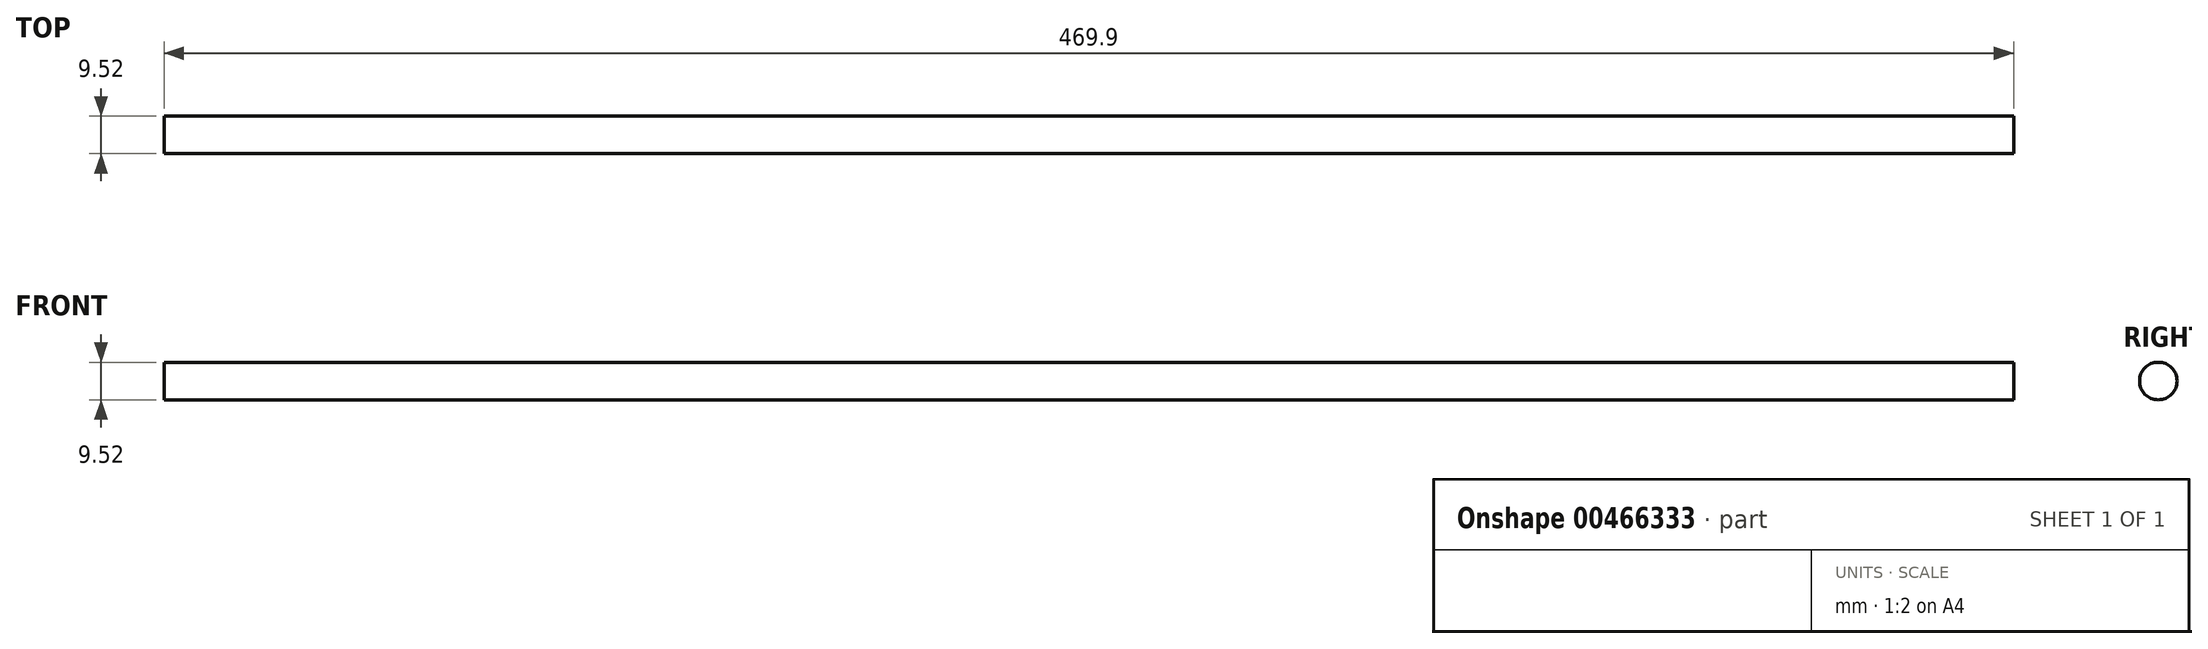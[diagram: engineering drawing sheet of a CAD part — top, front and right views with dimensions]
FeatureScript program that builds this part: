
annotation { "Feature Type Name" : "Feature", "Feature Type Description" : "" }
export const myFeature = defineFeature(function(context is Context, id is Id, definition is map)
    precondition{}
    {
        {
            var Q0;
            Q0=qCreatedBy(makeId("Right.planeOp"),FACE);
            var sketch = newSketch(context, id + "F0", { "sketchPlane" : qUnion([Q0])});
            skCircle(sketch, "E0", {"center": v(0, 0) * mm, "radius": 4.76 * mm});
            skSolve(sketch);
        }
        {
            var Q0;
            Q0=makeQuery(id+"F0.imprint","IMPRINT",FACE,{"disambiguationData":[TD([[makeQuery(id+"F0.imprint","IMPRINT",EDGE,{"derivedFrom":sQuery(id+"F0.wireOp",EDGE,"E0")}),1.0]])]});
            extrude(context, id + "F1", {"entities" : qUnion([Q0]), "depth" : 469.9 * mm});
        }
    });
